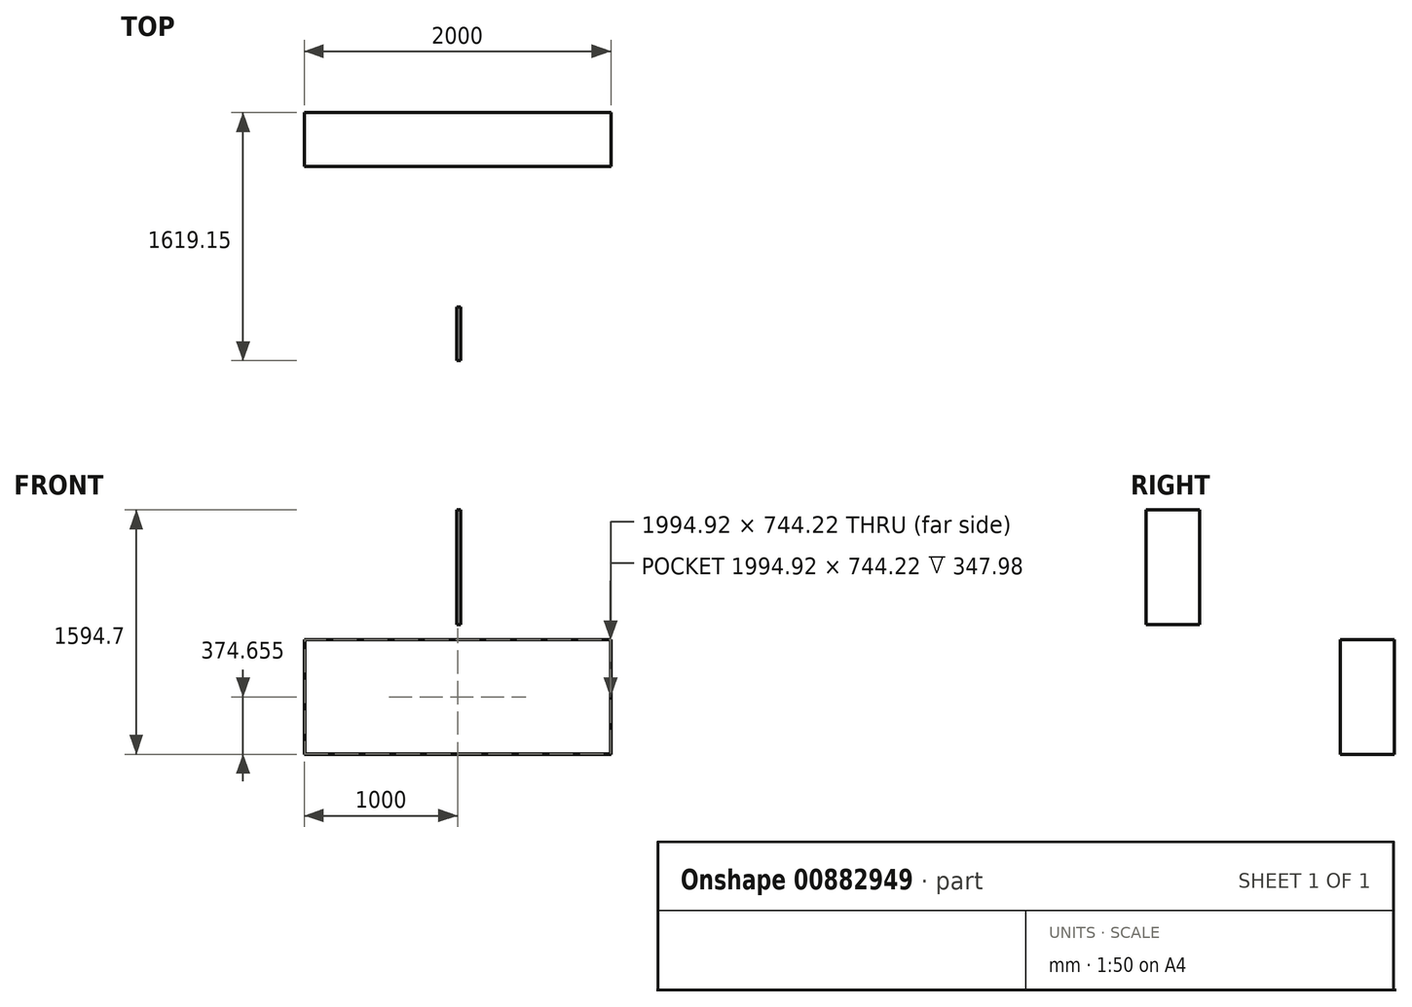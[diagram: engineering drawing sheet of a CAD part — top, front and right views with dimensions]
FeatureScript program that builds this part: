
annotation { "Feature Type Name" : "Feature", "Feature Type Description" : "" }
export const myFeature = defineFeature(function(context is Context, id is Id, definition is map)
    precondition{}
    {
        {
            var Q0;
            Q0=qCreatedBy(makeId("Front.planeOp"),FACE);
            var sketch = newSketch(context, id + "F0", { "sketchPlane" : qUnion([Q0])});
            skLineSegment(sketch, "E0.bottom", {"start": v(-995.57, 139.45) * mm, "end": v(1004.43, 139.45) * mm});
            skLineSegment(sketch, "E0.top", {"start": v(-995.57, -610.62) * mm, "end": v(1004.43, -610.62) * mm});
            skLineSegment(sketch, "E0.left", {"start": v(-995.57, 139.45) * mm, "end": v(-995.57, -610.62) * mm});
            skLineSegment(sketch, "E0.right", {"start": v(1004.43, 139.45) * mm, "end": v(1004.43, -610.62) * mm});
            skSolve(sketch);
        }
        {
            var Q0;
            Q0=sQuery(id+"F0.wireOp",EDGE,"E0.top");
            extrude(context, id + "F1", {"bodyType" : ToolBodyType.SURFACE, "surfaceEntities" : qUnion([Q0]), "oppositeDirection" : true, "depth" : 350.52 * mm, "offsetDistance" : 25.4 * mm});
        }
        {
            var Q0;
            Q0=makeQuery(id+"F1.opExtrude","SWEPT_FACE",FACE,{"disambiguationData":[OSD([sQuery(id+"F0.wireOp",EDGE,"E0.top")])]});
            extrude(context, id + "F2", {"entities" : qUnion([Q0]), "depth" : 749.3 * mm, "offsetDistance" : 25.4 * mm});
        }
        {
            var Q0;
            {var subQ0=sQuery(id+"F0.wireOp",EDGE,"E0.top");Q0=makeQuery(id+"F2.opExtrude","SWEPT_FACE",FACE,{"disambiguationData":[OSD([subQ0]),TDD([makeQuery(id+"F1.opExtrude","CAP_EDGE",EDGE,{"disambiguationData":[OSD([subQ0])],"isStart":true})])]});}
            shell(context, id + "F3", {"entities" : qUnion([Q0]), "thickness" : 2.54 * mm});
        }
        {
            var Q0;
            Q0=qCreatedBy(makeId("Right.planeOp"),FACE);
            var sketch = newSketch(context, id + "F4", { "sketchPlane" : qUnion([Q0])});
            skLineSegment(sketch, "E1.bottom", {"start": v(-918.63, 984.08) * mm, "end": v(-1268.63, 984.08) * mm});
            skLineSegment(sketch, "E1.top", {"start": v(-918.63, 234.78) * mm, "end": v(-1268.63, 234.78) * mm});
            skLineSegment(sketch, "E1.left", {"start": v(-918.63, 984.08) * mm, "end": v(-918.63, 234.78) * mm});
            skLineSegment(sketch, "E1.right", {"start": v(-1268.63, 984.08) * mm, "end": v(-1268.63, 234.78) * mm});
            skSolve(sketch);
        }
        {
            var Q0;
            Q0=makeQuery(id+"F4.imprint","IMPRINT",FACE,{"disambiguationData":[TD([[makeQuery(id+"F4.imprint","IMPRINT",EDGE,{"derivedFrom":sQuery(id+"F4.wireOp",EDGE,"E1.bottom")}),1.0]])]});
            extrude(context, id + "F5", {"entities" : qUnion([Q0]), "depth" : 25.4 * mm, "offsetDistance" : 25.4 * mm});
        }
    });
